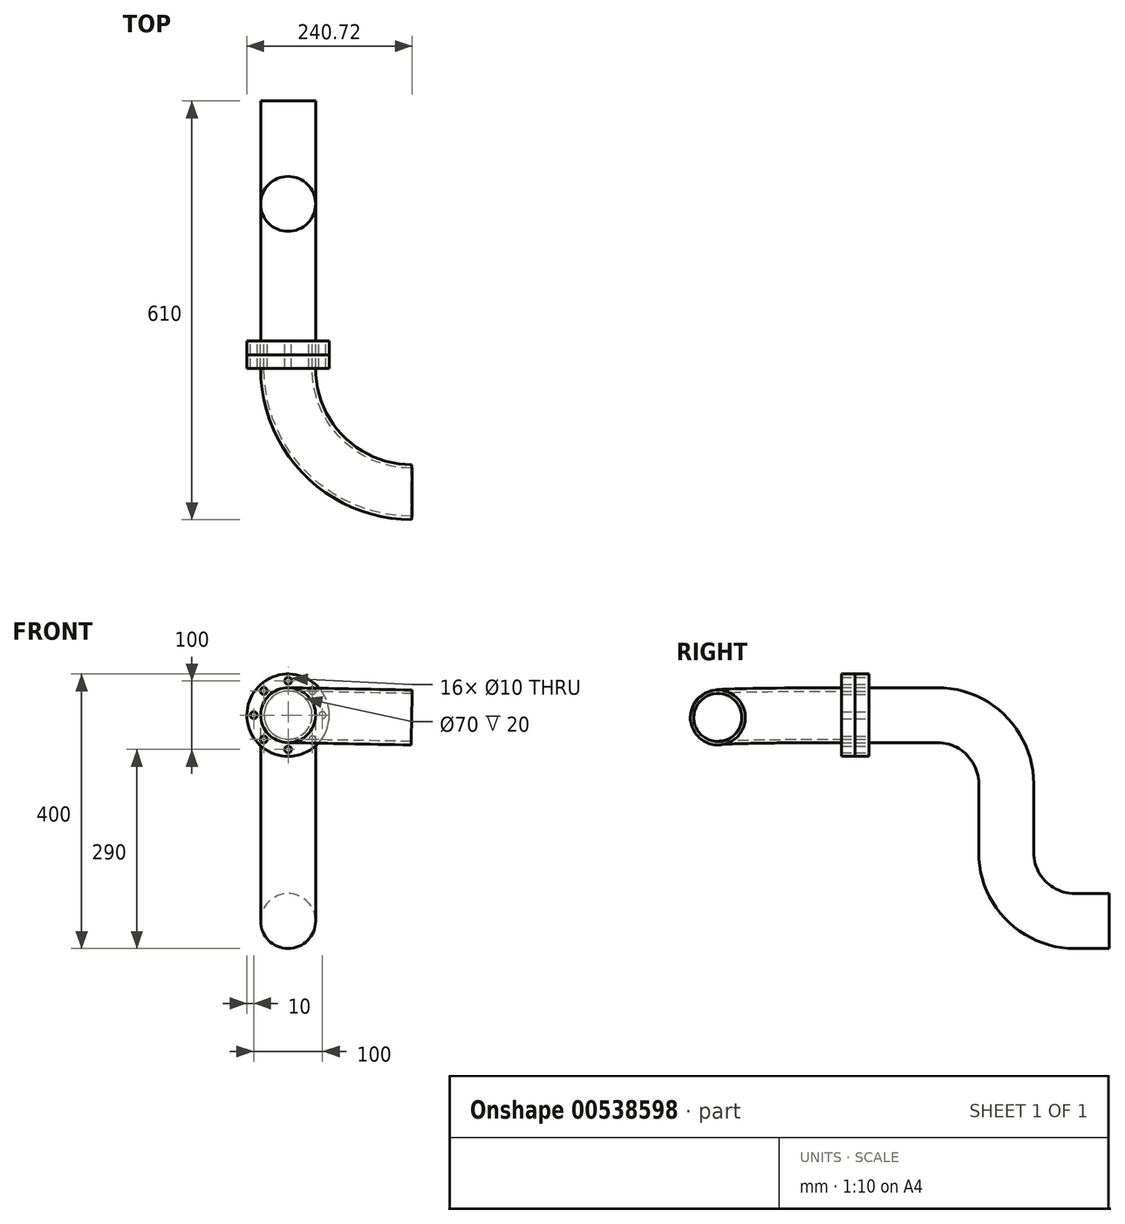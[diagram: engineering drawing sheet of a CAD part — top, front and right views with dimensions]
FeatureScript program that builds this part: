
annotation { "Feature Type Name" : "Feature", "Feature Type Description" : "" }
export const myFeature = defineFeature(function(context is Context, id is Id, definition is map)
    precondition{}
    {
        {
            var Q0;
            Q0=qCreatedBy(makeId("Front.planeOp"),FACE);
            var sketch = newSketch(context, id + "F0", { "sketchPlane" : qUnion([Q0])});
            skCircle(sketch, "E0", {"center": v(0, 0) * mm, "radius": 60 * mm});
            skCircle(sketch, "E1", {"center": v(0, 50) * mm, "radius": 5 * mm});
            skCircle(sketch, "E2.1.0", {"center": v(-35.36, 35.36) * mm, "radius": 5 * mm});
            skCircle(sketch, "E2.2.0", {"center": v(-50, 0) * mm, "radius": 5 * mm});
            skCircle(sketch, "E2.3.0", {"center": v(-35.36, -35.36) * mm, "radius": 5 * mm});
            skCircle(sketch, "E2.4.0", {"center": v(0, -50) * mm, "radius": 5 * mm});
            skCircle(sketch, "E2.5.0", {"center": v(35.36, -35.36) * mm, "radius": 5 * mm});
            skCircle(sketch, "E2.6.0", {"center": v(50, 0) * mm, "radius": 5 * mm});
            skCircle(sketch, "E2.7.0", {"center": v(35.36, 35.36) * mm, "radius": 5 * mm});
            skCircle(sketch, "E3", {"center": v(0, 0) * mm, "radius": 35 * mm});
            skSolve(sketch);
        }
        {
            var Q0;
            Q0 = qSketchRegion(id + "F0", true);
            extrude(context, id + "F1", {"entities" : qUnion([Q0]), "depth" : 20 * mm, "offsetDistance" : 25 * mm});
        }
        {
            var Q0;
            Q0=makeQuery(id+"F1.opExtrude","CAP_FACE",FACE,{"disambiguationData":[OSD([sQuery(id+"F0.wireOp",EDGE,"E0"),sQuery(id+"F0.wireOp",EDGE,"E1"),sQuery(id+"F0.wireOp",EDGE,"E2.1.0"),sQuery(id+"F0.wireOp",EDGE,"E2.2.0"),sQuery(id+"F0.wireOp",EDGE,"E2.3.0"),sQuery(id+"F0.wireOp",EDGE,"E2.4.0"),sQuery(id+"F0.wireOp",EDGE,"E2.5.0"),sQuery(id+"F0.wireOp",EDGE,"E2.6.0"),sQuery(id+"F0.wireOp",EDGE,"E2.7.0")])],"isStart":false});
            extrude(context, id + "F2", {"entities" : qUnion([Q0]), "depth" : 20 * mm, "offsetDistance" : 25 * mm});
        }
        {
            var Q0;
            Q0=qCreatedBy(makeId("Front.planeOp"),FACE);
            var sketch = newSketch(context, id + "F3", { "sketchPlane" : qUnion([Q0])});
            skCircle(sketch, "E4", {"center": v(0, 0) * mm, "radius": 40 * mm});
            skSolve(sketch);
        }
        {
            var Q0;
            Q0=qCreatedBy(makeId("Right.planeOp"),FACE);
            var sketch = newSketch(context, id + "F4", { "sketchPlane" : qUnion([Q0])});
            skLineSegment(sketch, "E5", {"start": v(0, 0) * mm, "end": v(100, 0) * mm});
            skLineSegment(sketch, "E6", {"start": v(200, -100) * mm, "end": v(200, -200) * mm});
            skLineSegment(sketch, "E7", {"start": v(300, -300) * mm, "end": v(350, -300) * mm});
            skPoint(sketch, "E8.visualSharp", {"position": v(200, 0) * mm});
            skArc(sketch, "E8.filletArc", {"start": v(200, -100) * mm, "mid": v(170.71, -29.29) * mm, "end": v(100, 0) * mm});
            skPoint(sketch, "E9.visualSharp", {"position": v(200, -300) * mm});
            skArc(sketch, "E9.filletArc", {"start": v(200, -200) * mm, "mid": v(229.29, -270.71) * mm, "end": v(300, -300) * mm});
            skSolve(sketch);
        }
        {
            var Q0;
            Q0=qCreatedBy(makeId("Front.planeOp"),FACE);
            var sketch = newSketch(context, id + "F5", { "sketchPlane" : qUnion([Q0])});
            skCircle(sketch, "E10", {"center": v(0, 0) * mm, "radius": 35 * mm});
            skSolve(sketch);
        }
        {
            var Q0;
            Q0=makeQuery(id+"F3.imprint","IMPRINT",FACE,{"disambiguationData":[TD([[makeQuery(id+"F3.imprint","IMPRINT",EDGE,{"derivedFrom":sQuery(id+"F3.wireOp",EDGE,"E4")}),1.0]])]});
            var Q1;
            Q1=makeQuery(id+"F5.imprint","IMPRINT",FACE,{"disambiguationData":[TD([[makeQuery(id+"F5.imprint","IMPRINT",EDGE,{"derivedFrom":sQuery(id+"F5.wireOp",EDGE,"E10")}),1.0]])]});
            var Q2;
            Q2 = qConstructionFilter(qBodyType(qCreatedBy(id + "F4" ,EDGE), BodyType.WIRE), ConstructionObject.NO);
            sweep(context, id + "F6", {"operationType" : NewBodyOperationType.ADD, "profiles" : qUnion([Q0, Q1]), "path" : qUnion([Q2])});
        }
        {
            var Q0;
            Q0=makeQuery(id+"F2.opExtrude","CAP_FACE",FACE,{"disambiguationData":[OSD([sQuery(id+"F0.wireOp",EDGE,"E0"),sQuery(id+"F0.wireOp",EDGE,"E1"),sQuery(id+"F0.wireOp",EDGE,"E2.1.0"),sQuery(id+"F0.wireOp",EDGE,"E2.2.0"),sQuery(id+"F0.wireOp",EDGE,"E2.3.0"),sQuery(id+"F0.wireOp",EDGE,"E2.4.0"),sQuery(id+"F0.wireOp",EDGE,"E2.5.0"),sQuery(id+"F0.wireOp",EDGE,"E2.6.0"),sQuery(id+"F0.wireOp",EDGE,"E2.7.0"),sQuery(id+"F0.wireOp",EDGE,"E3")])],"isStart":false});
            var sketch = newSketch(context, id + "F7", { "sketchPlane" : qUnion([Q0])});
            skCircle(sketch, "E11", {"center": v(0, 0) * mm, "radius": 35 * mm});
            skCircle(sketch, "E12", {"center": v(0, 0) * mm, "radius": 40 * mm});
            skLineSegment(sketch, "E13", {"start": v(182.1, 109.63) * mm, "end": v(178.8, -65.15) * mm, "construction": true});
            skSolve(sketch);
        }
        {
            var Q0;
            Q0 = qSketchRegion(id + "F7", true);
            var Q1;
            Q1=sQuery(id+"F7.wireOp",EDGE,"E13");
            revolve(context, id + "F8", {"operationType" : NewBodyOperationType.ADD, "entities" : qUnion([Q0]), "axis" : qUnion([Q1]), "revolveType" : RevolveType.ONE_DIRECTION, "oppositeDirection" : true, "angle" : 90 * degree});
        }
    });
